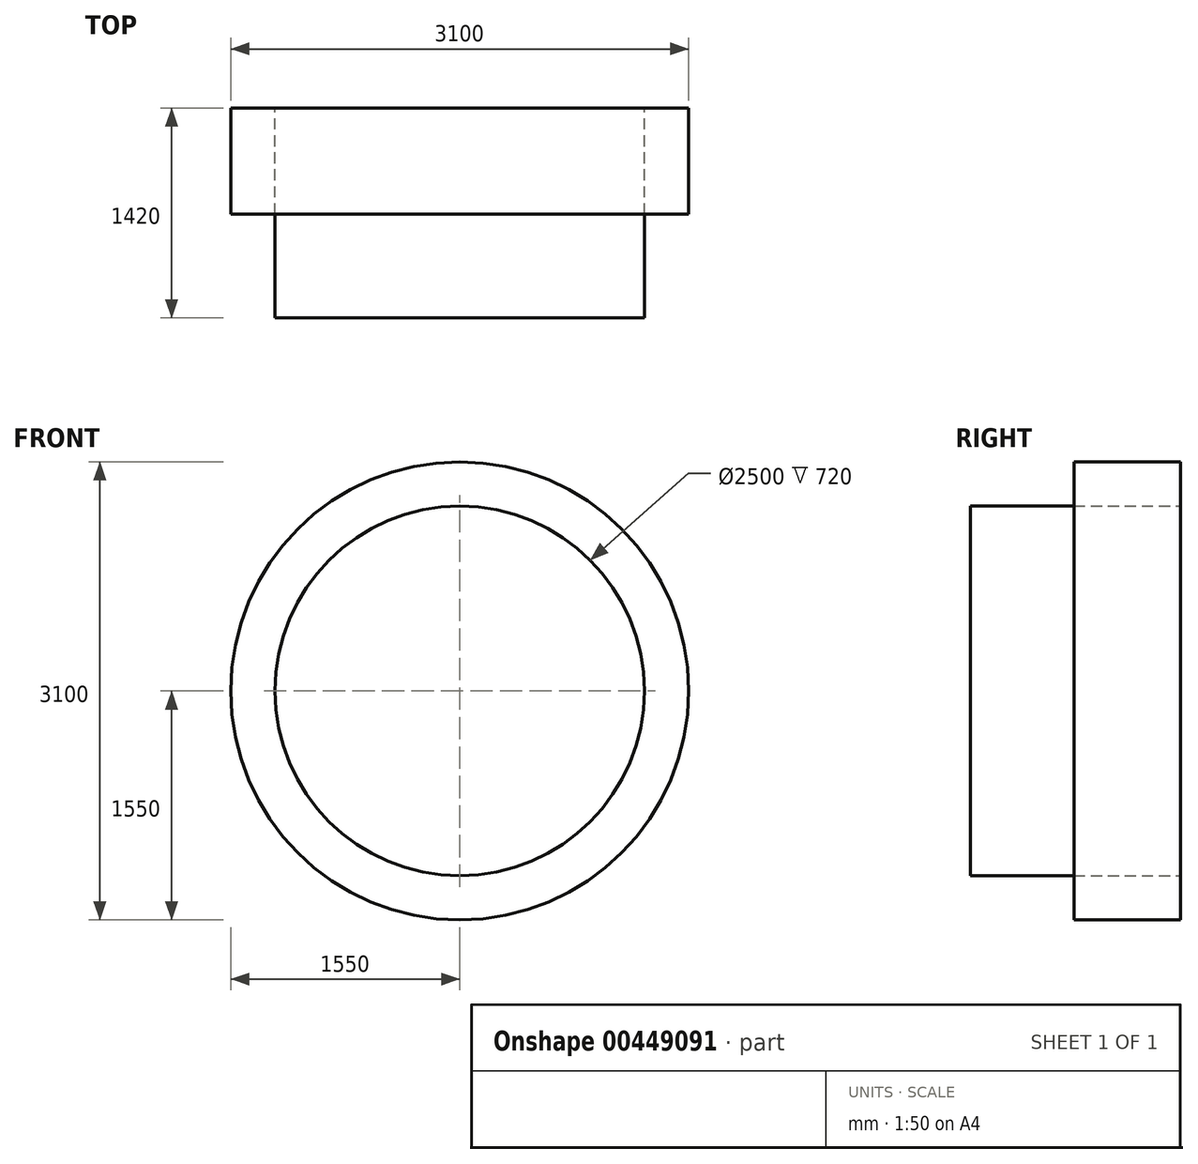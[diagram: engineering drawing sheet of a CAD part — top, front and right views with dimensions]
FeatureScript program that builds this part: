
annotation { "Feature Type Name" : "Feature", "Feature Type Description" : "" }
export const myFeature = defineFeature(function(context is Context, id is Id, definition is map)
    precondition{}
    {
        {
            var Q0;
            Q0=qCreatedBy(makeId("Front.planeOp"),FACE);
            var sketch = newSketch(context, id + "F0", { "sketchPlane" : qUnion([Q0])});
            skCircle(sketch, "E0", {"center": v(0, 0) * mm, "radius": 1250 * mm});
            skCircle(sketch, "E1.0", {"center": v(0, 0) * mm, "radius": 1550 * mm});
            skSolve(sketch);
        }
        {
            var Q0;
            Q0=makeQuery(id+"F0.imprint","IMPRINT",FACE,{"disambiguationData":[TD([[makeQuery(id+"F0.imprint","IMPRINT",EDGE,{"derivedFrom":sQuery(id+"F0.wireOp",EDGE,"E0")}),-1.0]])]});
            extrude(context, id + "F1", {"entities" : qUnion([Q0]), "depth" : 720 * mm});
        }
        {
            var Q0;
            Q0=makeQuery(id+"F1.opExtrude","CAP_FACE",FACE,{"disambiguationData":[OSD([sQuery(id+"F0.wireOp",EDGE,"E0"),sQuery(id+"F0.wireOp",EDGE,"E1.0")])],"isStart":false});
            var sketch = newSketch(context, id + "F2", { "sketchPlane" : qUnion([Q0])});
            skSolve(sketch);
        }
        {
            var Q0;
            Q0=makeQuery(id+"F2.imprint","IMPRINT",FACE,{"disambiguationData":[TD([[makeQuery(id+"F2.imprint","IMPRINT",EDGE,{"derivedFrom":makeQuery(id+"F1.opExtrude","CAP_EDGE",EDGE,{"disambiguationData":[OSD([sQuery(id+"F0.wireOp",EDGE,"E0")])],"isStart":false})}),1.0]])]});
            extrude(context, id + "F3", {"entities" : qUnion([Q0]), "depth" : 700 * mm});
        }
    });
